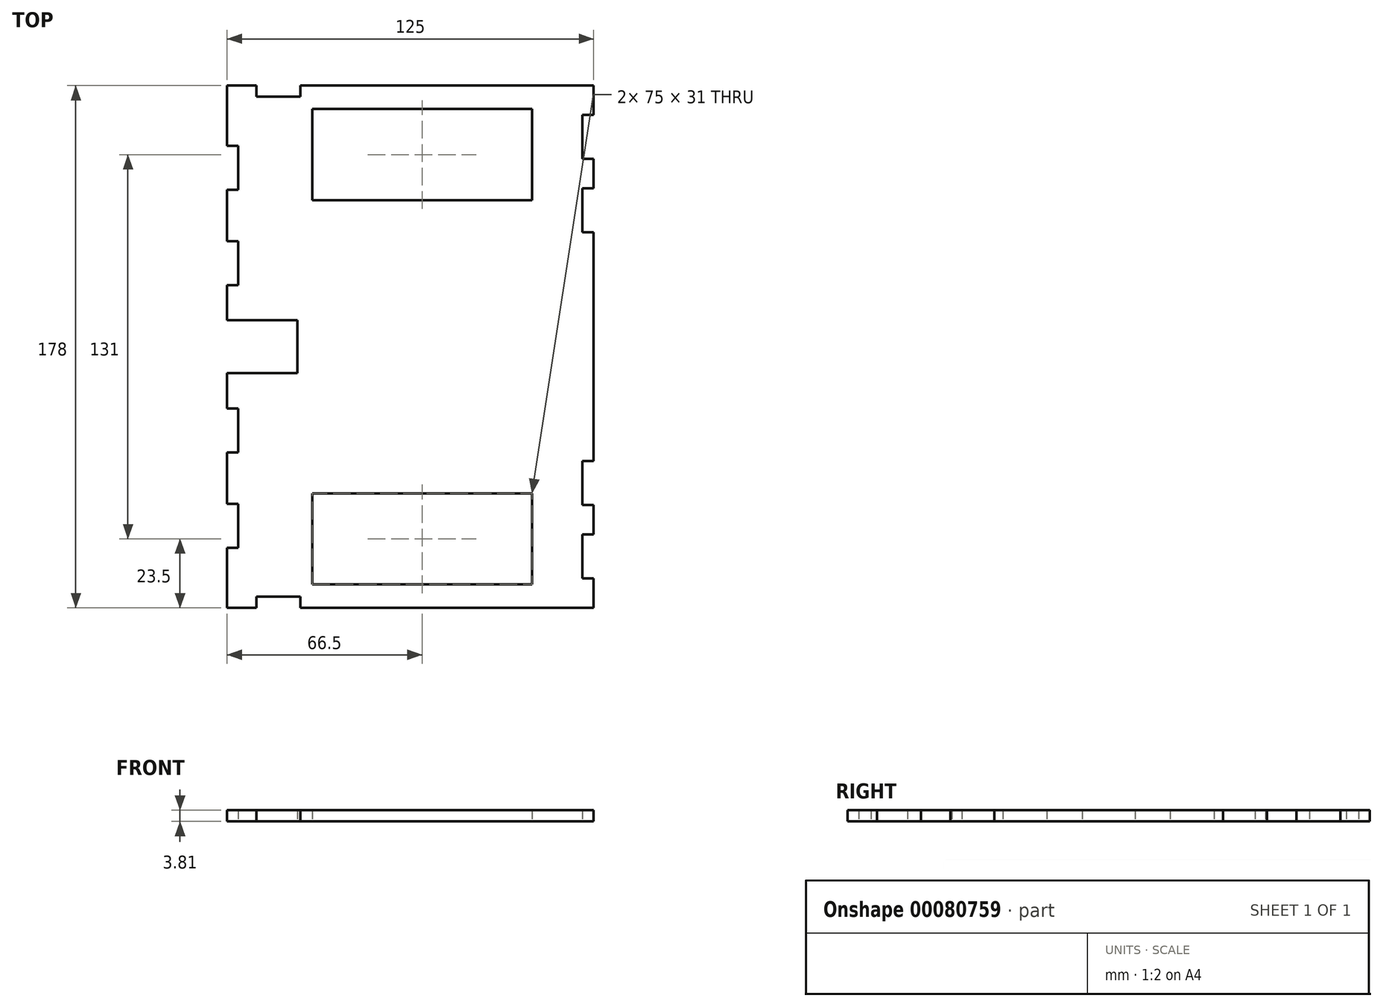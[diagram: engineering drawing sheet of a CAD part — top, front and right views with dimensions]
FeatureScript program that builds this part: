
annotation { "Feature Type Name" : "Feature", "Feature Type Description" : "" }
export const myFeature = defineFeature(function(context is Context, id is Id, definition is map)
    precondition{}
    {
        {
            var Q0;
            Q0=qCreatedBy(makeId("Top.planeOp"),FACE);
            var sketch = newSketch(context, id + "F0", { "sketchPlane" : qUnion([Q0])});
            skLineSegment(sketch, "E0.bottom", {"start": v(62.5, 89) * mm, "end": v(-62.5, 89) * mm});
            skLineSegment(sketch, "E0.top", {"start": v(62.5, -89) * mm, "end": v(-62.5, -89) * mm});
            skLineSegment(sketch, "E0.left", {"start": v(62.5, 89) * mm, "end": v(62.5, -89) * mm});
            skLineSegment(sketch, "E0.right", {"start": v(-62.5, 89) * mm, "end": v(-62.5, -89) * mm});
            skPoint(sketch, "E0.middle", {"position": v(0, 0) * mm});
            skLineSegment(sketch, "E1.bottom", {"start": v(41.5, 81) * mm, "end": v(-33.5, 81) * mm});
            skLineSegment(sketch, "E1.top", {"start": v(41.5, 50) * mm, "end": v(-33.5, 50) * mm});
            skLineSegment(sketch, "E1.left", {"start": v(41.5, 81) * mm, "end": v(41.5, 50) * mm});
            skLineSegment(sketch, "E1.right", {"start": v(-33.5, 81) * mm, "end": v(-33.5, 50) * mm});
            skPoint(sketch, "E1.middle", {"position": v(4, 65.5) * mm});
            skLineSegment(sketch, "E2", {"start": v(-62.5, 0) * mm, "end": v(62.5, 0) * mm, "construction": true});
            skLineSegment(sketch, "E3.MirrorCS", {"start": v(-33.5, -81) * mm, "end": v(-33.5, -50) * mm});
            skLineSegment(sketch, "E4.MirrorCS", {"start": v(41.5, -81) * mm, "end": v(-33.5, -81) * mm});
            skLineSegment(sketch, "E5.MirrorCS", {"start": v(41.5, -81) * mm, "end": v(41.5, -50) * mm});
            skLineSegment(sketch, "E6.MirrorCS", {"start": v(41.5, -50) * mm, "end": v(-33.5, -50) * mm});
            skLineSegment(sketch, "E7", {"start": v(-62.5, 9) * mm, "end": v(-38.5, 9) * mm});
            skLineSegment(sketch, "E8", {"start": v(-38.5, 9) * mm, "end": v(-38.5, 0) * mm});
            skLineSegment(sketch, "E9.MirrorCS", {"start": v(-38.5, -9) * mm, "end": v(-38.5, 0) * mm});
            skLineSegment(sketch, "E10.MirrorCS", {"start": v(-62.5, -9) * mm, "end": v(-38.5, -9) * mm});
            skLineSegment(sketch, "E11", {"start": v(-52.5, -89) * mm, "end": v(-52.5, -85.19) * mm});
            skLineSegment(sketch, "E12", {"start": v(-52.5, -85.19) * mm, "end": v(-37.5, -85.19) * mm});
            skLineSegment(sketch, "E13", {"start": v(-37.5, -85.19) * mm, "end": v(-37.5, -89) * mm});
            skLineSegment(sketch, "E14.MirrorCS", {"start": v(-52.5, 85.19) * mm, "end": v(-37.5, 85.19) * mm});
            skLineSegment(sketch, "E15.MirrorCS", {"start": v(-52.5, 89) * mm, "end": v(-52.5, 85.19) * mm});
            skLineSegment(sketch, "E16.MirrorCS", {"start": v(-37.5, 85.19) * mm, "end": v(-37.5, 89) * mm});
            skLineSegment(sketch, "E17", {"start": v(62.5, 79) * mm, "end": v(58.69, 79) * mm});
            skLineSegment(sketch, "E18", {"start": v(58.69, 79) * mm, "end": v(58.69, 64) * mm});
            skLineSegment(sketch, "E19", {"start": v(58.69, 64) * mm, "end": v(62.5, 64) * mm});
            skLineSegment(sketch, "E20", {"start": v(62.5, 54) * mm, "end": v(58.69, 54) * mm});
            skLineSegment(sketch, "E21", {"start": v(58.69, 54) * mm, "end": v(58.69, 39) * mm});
            skLineSegment(sketch, "E22", {"start": v(58.7, 39) * mm, "end": v(62.5, 39) * mm});
            skLineSegment(sketch, "E23.MirrorCS", {"start": v(58.7, -39) * mm, "end": v(62.5, -39) * mm});
            skLineSegment(sketch, "E24.MirrorCS", {"start": v(58.7, -54) * mm, "end": v(58.7, -39) * mm});
            skLineSegment(sketch, "E25.MirrorCS", {"start": v(62.5, -54) * mm, "end": v(58.69, -54) * mm});
            skLineSegment(sketch, "E26.MirrorCS", {"start": v(58.69, -64) * mm, "end": v(62.5, -64) * mm});
            skLineSegment(sketch, "E27.MirrorCS", {"start": v(58.7, -79) * mm, "end": v(58.7, -64) * mm});
            skLineSegment(sketch, "E28.MirrorCS", {"start": v(62.5, -79) * mm, "end": v(58.69, -79) * mm});
            skLineSegment(sketch, "E29", {"start": v(-62.5, 68.5) * mm, "end": v(-58.69, 68.5) * mm});
            skLineSegment(sketch, "E30", {"start": v(-58.7, 68.5) * mm, "end": v(-58.7, 53.5) * mm});
            skLineSegment(sketch, "E31", {"start": v(-58.69, 53.5) * mm, "end": v(-62.5, 53.5) * mm});
            skLineSegment(sketch, "E32", {"start": v(-62.5, 36) * mm, "end": v(-58.69, 36) * mm});
            skLineSegment(sketch, "E33", {"start": v(-58.7, 36) * mm, "end": v(-58.7, 21) * mm});
            skLineSegment(sketch, "E34", {"start": v(-58.69, 21) * mm, "end": v(-62.5, 21) * mm});
            skLineSegment(sketch, "E35.MirrorCS", {"start": v(-58.69, -36) * mm, "end": v(-58.69, -21) * mm});
            skLineSegment(sketch, "E36.MirrorCS", {"start": v(-58.69, -21) * mm, "end": v(-62.5, -21) * mm});
            skLineSegment(sketch, "E37.MirrorCS", {"start": v(-62.5, -36) * mm, "end": v(-58.69, -36) * mm});
            skLineSegment(sketch, "E38.MirrorCS", {"start": v(-58.69, -53.5) * mm, "end": v(-62.5, -53.5) * mm});
            skLineSegment(sketch, "E39.MirrorCS", {"start": v(-58.7, -68.5) * mm, "end": v(-58.7, -53.5) * mm});
            skLineSegment(sketch, "E40.MirrorCS", {"start": v(-62.5, -68.5) * mm, "end": v(-58.69, -68.5) * mm});
            skSolve(sketch);
        }
        {
            var Q0;
            Q0=makeQuery(id+"F0.imprint","IMPRINT",FACE,{"disambiguationData":[TD([[makeQuery(id+"F0.imprint","IMPRINT",EDGE,{"derivedFrom":sQuery(id+"F0.wireOp",EDGE,"E0.bottom")}),1.0]])]});
            extrude(context, id + "F1", {"entities" : qUnion([Q0]), "depth" : 3.8 * mm});
        }
    });
